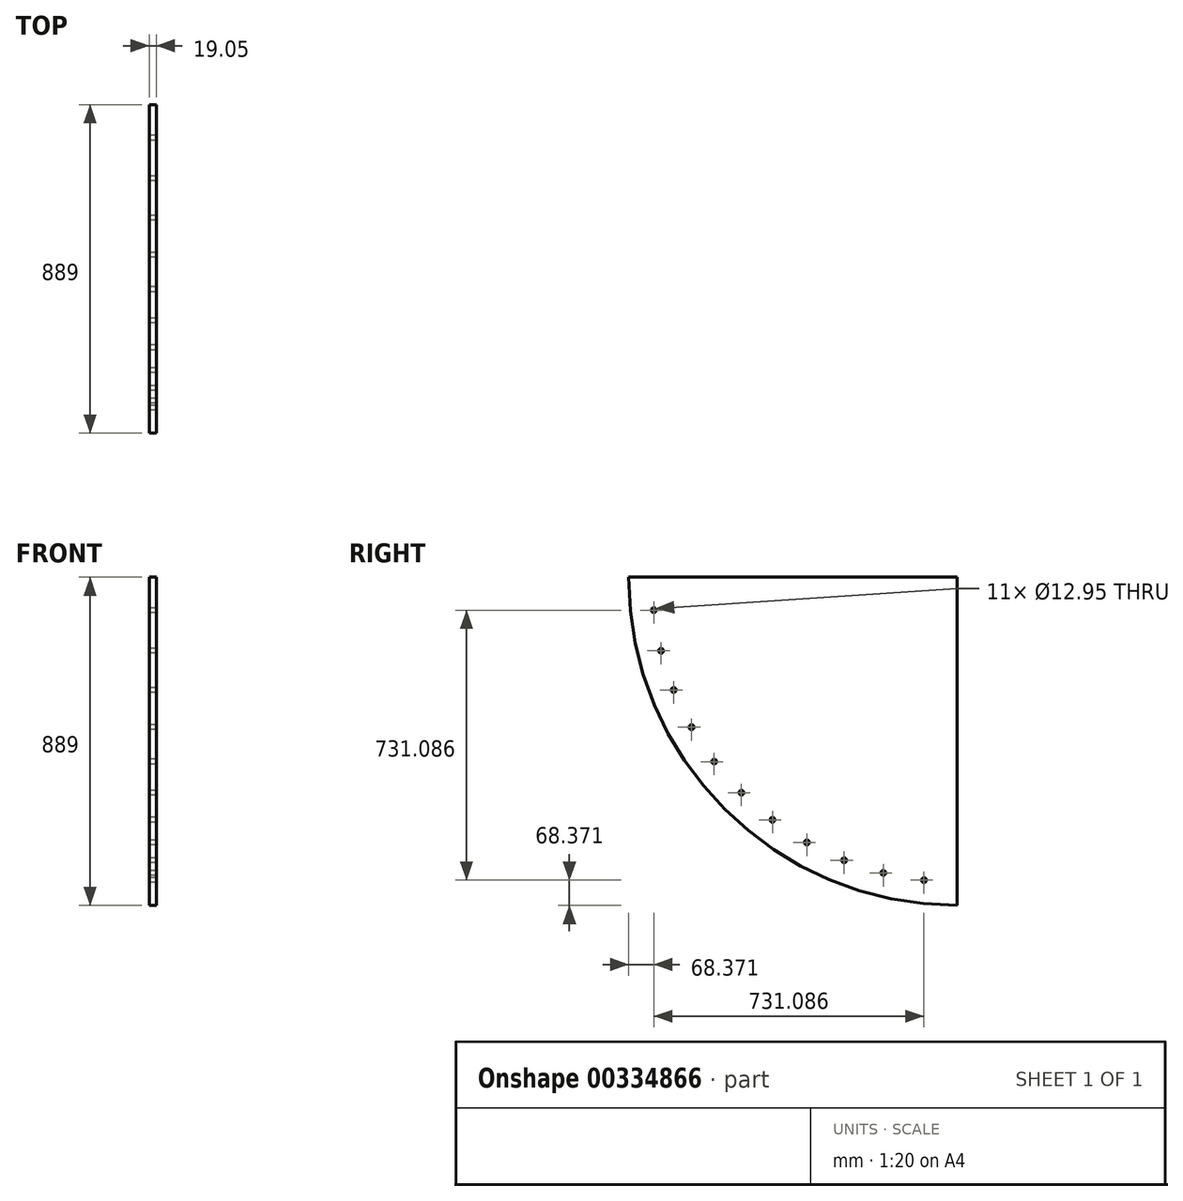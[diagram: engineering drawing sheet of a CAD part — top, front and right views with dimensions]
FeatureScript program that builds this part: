
annotation { "Feature Type Name" : "Feature", "Feature Type Description" : "" }
export const myFeature = defineFeature(function(context is Context, id is Id, definition is map)
    precondition{}
    {
        {
            var Q0;
            Q0=qCreatedBy(makeId("Right.planeOp"),FACE);
            var sketch = newSketch(context, id + "F0", { "sketchPlane" : qUnion([Q0])});
            skArc(sketch, "E0", {"start": v(-889, 0) * mm, "mid": v(-628.62, -628.62) * mm, "end": v(0, -889) * mm});
            skLineSegment(sketch, "E1", {"start": v(0, -889) * mm, "end": v(0, 0) * mm});
            skLineSegment(sketch, "E2", {"start": v(-889, 0) * mm, "end": v(0, 0) * mm});
            skCircle(sketch, "E3", {"center": v(-89.54, -820.63) * mm, "radius": 6.48 * mm});
            skCircle(sketch, "E4.1.0", {"center": v(-199.45, -801.04) * mm, "radius": 6.48 * mm});
            skCircle(sketch, "E4.2.0", {"center": v(-305.71, -766.8) * mm, "radius": 6.48 * mm});
            skCircle(sketch, "E4.3.0", {"center": v(-406.38, -718.54) * mm, "radius": 6.48 * mm});
            skCircle(sketch, "E4.4.0", {"center": v(-499.62, -657.14) * mm, "radius": 6.48 * mm});
            skCircle(sketch, "E4.5.0", {"center": v(-583.72, -583.72) * mm, "radius": 6.48 * mm});
            skCircle(sketch, "E4.6.0", {"center": v(-657.14, -499.62) * mm, "radius": 6.48 * mm});
            skCircle(sketch, "E4.7.0", {"center": v(-718.54, -406.38) * mm, "radius": 6.48 * mm});
            skCircle(sketch, "E4.8.0", {"center": v(-766.8, -305.71) * mm, "radius": 6.48 * mm});
            skCircle(sketch, "E4.9.0", {"center": v(-801.04, -199.45) * mm, "radius": 6.48 * mm});
            skCircle(sketch, "E5.1.10.0", {"center": v(-820.63, -89.54) * mm, "radius": 6.48 * mm});
            skCircle(sketch, "E6.1.12.0", {"center": v(-814.7, 133.15) * mm, "radius": 6.48 * mm});
            skLineSegment(sketch, "E7", {"start": v(0, 0) * mm, "end": v(-628.62, -628.62) * mm, "construction": true});
            skSolve(sketch);
        }
        {
            var Q0;
            Q0=makeQuery(id+"F0.imprint","IMPRINT",FACE,{"disambiguationData":[TD([[makeQuery(id+"F0.imprint","IMPRINT",EDGE,{"derivedFrom":sQuery(id+"F0.wireOp",EDGE,"E0")}),1.0]])]});
            extrude(context, id + "F1", {"entities" : qUnion([Q0]), "depth" : 19.05 * mm});
        }
    });
